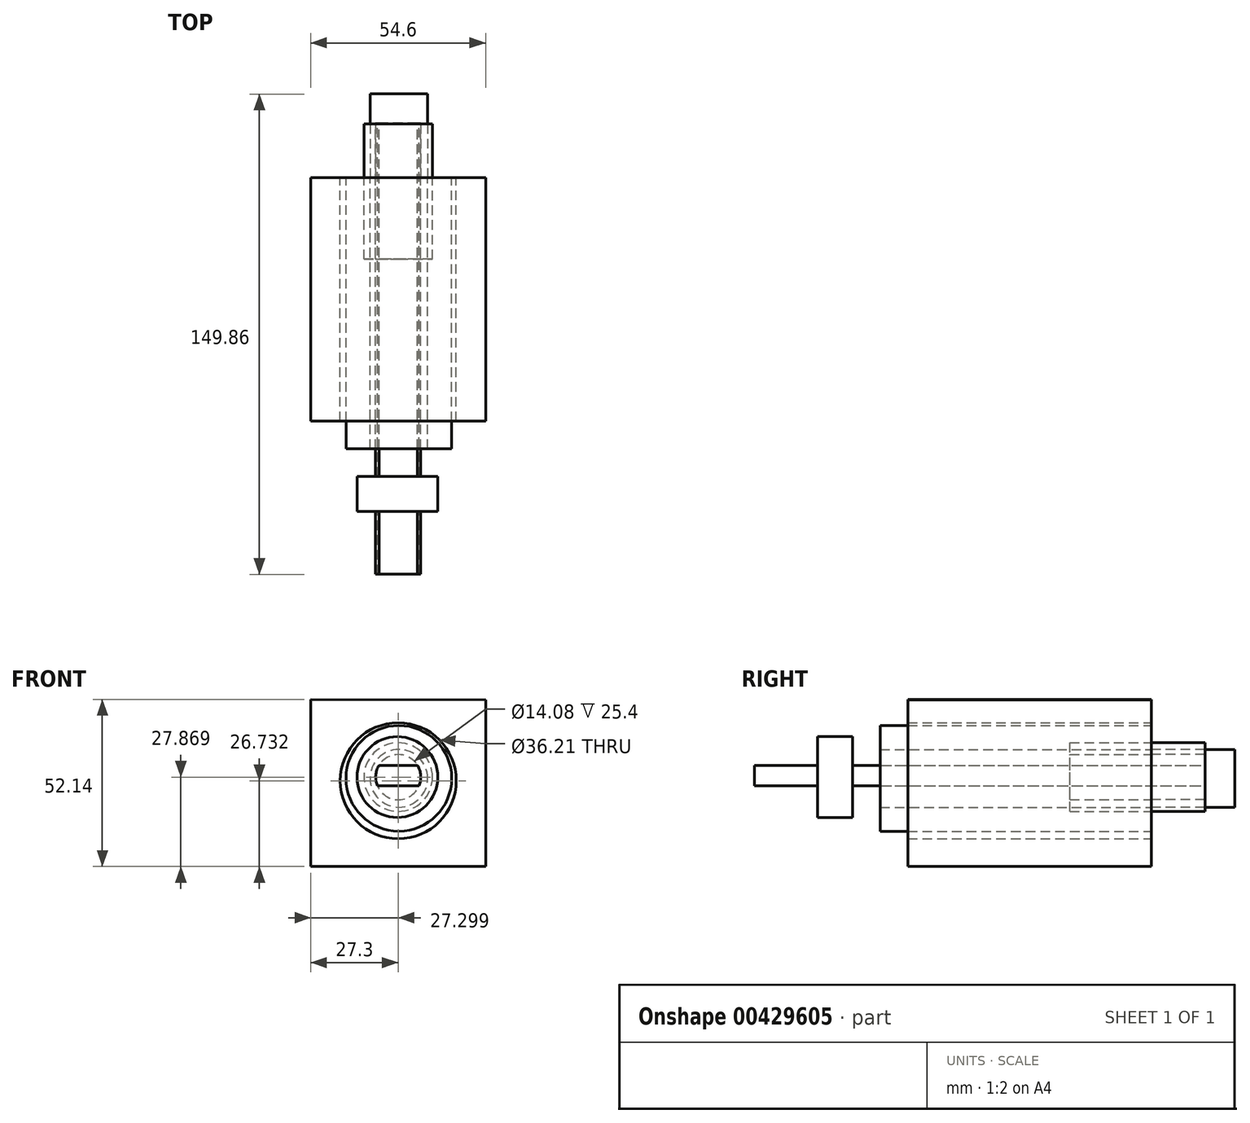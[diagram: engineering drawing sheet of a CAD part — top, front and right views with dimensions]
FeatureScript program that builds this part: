
annotation { "Feature Type Name" : "Feature", "Feature Type Description" : "" }
export const myFeature = defineFeature(function(context is Context, id is Id, definition is map)
    precondition{}
    {
        {
            var Q0;
            Q0=qCreatedBy(makeId("Front.planeOp"),FACE);
            var sketch = newSketch(context, id + "F0", { "sketchPlane" : qUnion([Q0])});
            skLineSegment(sketch, "E0", {"start": v(-64.84, 66.93) * mm, "end": v(-64.84, 14.79) * mm});
            skLineSegment(sketch, "E1", {"start": v(-64.84, 14.79) * mm, "end": v(-10.24, 14.79) * mm});
            skLineSegment(sketch, "E2", {"start": v(-10.24, 14.79) * mm, "end": v(-10.24, 66.74) * mm});
            skLineSegment(sketch, "E3", {"start": v(-64.84, 66.93) * mm, "end": v(-10.24, 66.74) * mm});
            skCircle(sketch, "E4", {"center": v(-37.54, 41.52) * mm, "radius": 18.1 * mm});
            skSolve(sketch);
        }
        {
            var Q0;
            Q0=makeQuery(id+"F0.imprint","IMPRINT",FACE,{"disambiguationData":[TD([[makeQuery(id+"F0.imprint","IMPRINT",EDGE,{"derivedFrom":sQuery(id+"F0.wireOp",EDGE,"E0")}),1.0]])]});
            extrude(context, id + "F1", {"entities" : qUnion([Q0]), "depth" : 75.95 * mm});
        }
        {
            var Q0;
            Q0=qCreatedBy(makeId("Front.planeOp"),FACE);
            var sketch = newSketch(context, id + "F2", { "sketchPlane" : qUnion([Q0])});
            skCircle(sketch, "E5", {"center": v(-37.35, 42.28) * mm, "radius": 16.5 * mm});
            skCircle(sketch, "E6", {"center": v(-37.35, 42.28) * mm, "radius": 9 * mm});
            skSolve(sketch);
        }
        {
            var Q0;
            Q0=makeQuery(id+"F2.imprint","IMPRINT",FACE,{"disambiguationData":[TD([[makeQuery(id+"F2.imprint","IMPRINT",EDGE,{"derivedFrom":sQuery(id+"F2.wireOp",EDGE,"E5")}),1.0]])]});
            extrude(context, id + "F3", {"entities" : qUnion([Q0]), "depth" : 84.58 * mm});
        }
        {
            var Q0;
            Q0=qCreatedBy(makeId("Front.planeOp"),FACE);
            var sketch = newSketch(context, id + "F4", { "sketchPlane" : qUnion([Q0])});
            skCircle(sketch, "E7", {"center": v(-37.54, 42.66) * mm, "radius": 7.04 * mm});
            skCircle(sketch, "E8", {"center": v(-37.54, 42.66) * mm, "radius": 10.7 * mm});
            skLineSegment(sketch, "E9", {"start": v(-31.56, 46.36) * mm, "end": v(-43.53, 46.36) * mm});
            skLineSegment(sketch, "E10", {"start": v(-44.02, 39.91) * mm, "end": v(-31.06, 39.91) * mm});
            skLineSegment(sketch, "E11", {"start": v(-35.76, 46.36) * mm, "end": v(-35.76, 49.47) * mm});
            skLineSegment(sketch, "E12", {"start": v(-35.76, 39.91) * mm, "end": v(-35.76, 35.85) * mm});
            skLineSegment(sketch, "E13", {"start": v(-39.55, 46.36) * mm, "end": v(-39.55, 49.4) * mm});
            skLineSegment(sketch, "E14", {"start": v(-39.93, 39.91) * mm, "end": v(-39.93, 36.04) * mm});
            skSolve(sketch);
        }
        {
            var Q0;
            Q0=makeQuery(id+"F4.imprint","IMPRINT",FACE,{"disambiguationData":[TD([[makeQuery(id+"F4.imprint","IMPRINT",EDGE,{"derivedFrom":sQuery(id+"F4.wireOp",EDGE,"E7")}),1.0]])]});
            extrude(context, id + "F5", {"entities" : qUnion([Q0]), "depth" : 123.7 * mm, "hasSecondDirection" : true, "secondDirectionOppositeDirection" : true, "secondDirectionDepth" : 17.02 * mm});
        }
        {
            var Q0;
            Q0 = qSketchRegion(id + "F4", true);
            extrude(context, id + "F6", {"entities" : qUnion([Q0]), "depth" : 25.4 * mm});
        }
        {
            var Q0;
            Q0 = qSketchRegion(id + "F4", true);
            extrude(context, id + "F7", {"entities" : qUnion([Q0]), "oppositeDirection" : true, "depth" : 16.76 * mm});
        }
        {
            var Q0;
            Q0=qCreatedBy(makeId("Top.planeOp"),FACE);
            var sketch = newSketch(context, id + "F8", { "sketchPlane" : qUnion([Q0])});
            skCircle(sketch, "E15", {"center": v(-37.89, 7.94) * mm, "radius": 6.25 * mm});
            skSolve(sketch);
        }
        {
            var Q0;
            Q0 = qSketchRegion(id + "F8", true);
            extrude(context, id + "F9", {"entities" : qUnion([Q0]), "depth" : 25.4 * mm});
        }
        {
            var Q0;
            Q0=makeQuery(id+"F9.opExtrude","SWEPT_BODY",BODY,{"disambiguationData":[OSD([sQuery(id+"F8.wireOp",EDGE,"E15")])]});
            deleteBodies(context, id + "F10", {"entities" : qUnion([Q0])});
        }
        {
            var Q0;
            Q0=makeQuery(id+"F2.imprint","IMPRINT",FACE,{"disambiguationData":[TD([[makeQuery(id+"F2.imprint","IMPRINT",EDGE,{"derivedFrom":sQuery(id+"F2.wireOp",EDGE,"E6")}),1.0]])]});
            extrude(context, id + "F11", {"entities" : qUnion([Q0]), "oppositeDirection" : true, "depth" : 26.16 * mm});
        }
        {
            var Q0;
            Q0=qCreatedBy(makeId("Front.planeOp"),FACE);
            var sketch = newSketch(context, id + "F12", { "sketchPlane" : qUnion([Q0])});
            skCircle(sketch, "E16", {"center": v(-37.8, 42.66) * mm, "radius": 12.6 * mm});
            skLineSegment(sketch, "E17", {"start": v(-38.5, 55.24) * mm, "end": v(-43.24, 49.1) * mm});
            skLineSegment(sketch, "E18", {"start": v(-43.24, 49.1) * mm, "end": v(-48.64, 49.1) * mm});
            skLineSegment(sketch, "E19", {"start": v(-48.64, 49.1) * mm, "end": v(-46.47, 42.47) * mm});
            skLineSegment(sketch, "E20", {"start": v(-46.47, 42.47) * mm, "end": v(-48.64, 36.21) * mm});
            skLineSegment(sketch, "E21", {"start": v(-48.64, 36.21) * mm, "end": v(-43.24, 34.34) * mm});
            skLineSegment(sketch, "E22", {"start": v(-43.24, 34.34) * mm, "end": v(-38.5, 30.07) * mm});
            skLineSegment(sketch, "E23", {"start": v(-38.5, 30.07) * mm, "end": v(-32.82, 34.34) * mm});
            skLineSegment(sketch, "E24", {"start": v(-32.82, 34.34) * mm, "end": v(-26.98, 36.21) * mm});
            skLineSegment(sketch, "E25", {"start": v(-26.98, 36.21) * mm, "end": v(-28.98, 42.47) * mm});
            skLineSegment(sketch, "E26", {"start": v(-28.98, 42.47) * mm, "end": v(-26.98, 49.1) * mm});
            skLineSegment(sketch, "E27", {"start": v(-26.98, 49.1) * mm, "end": v(-32.82, 50.87) * mm});
            skLineSegment(sketch, "E28", {"start": v(-32.82, 50.87) * mm, "end": v(-38.5, 55.24) * mm});
            skSolve(sketch);
        }
        {
            var Q0;
            Q0 = qSketchRegion(id + "F12", true);
            extrude(context, id + "F13", {"entities" : qUnion([Q0]), "operationType" : NewBodyOperationType.ADD, "depth" : 104.14 * mm, "hasSecondDirection" : true, "secondDirectionOppositeDirection" : false, "secondDirectionDepth" : 93.22 * mm});
        }
    });
